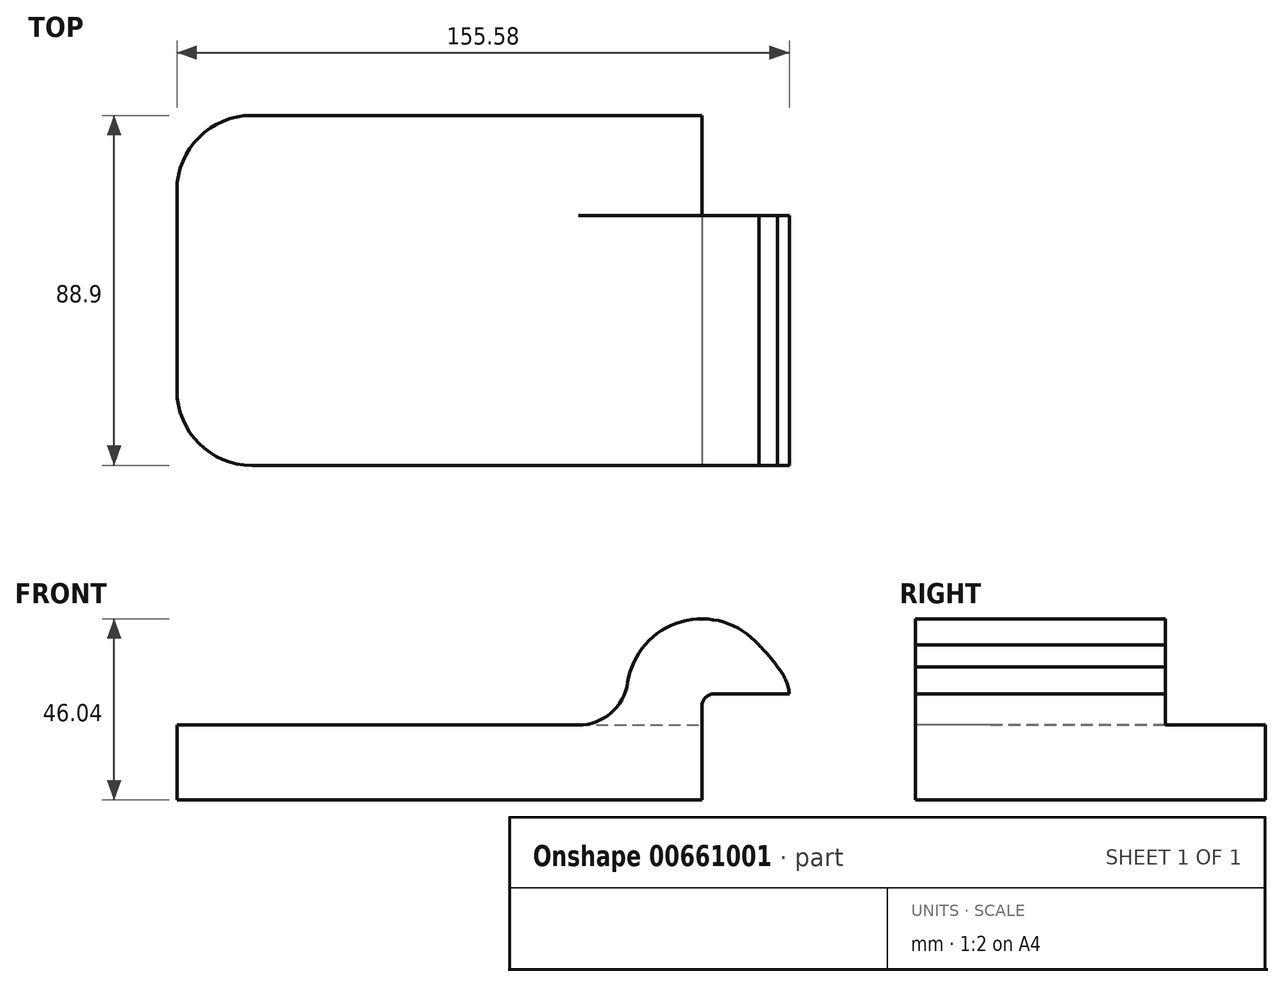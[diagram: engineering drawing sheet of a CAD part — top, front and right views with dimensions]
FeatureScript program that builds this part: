
annotation { "Feature Type Name" : "Feature", "Feature Type Description" : "" }
export const myFeature = defineFeature(function(context is Context, id is Id, definition is map)
    precondition{}
    {
        {
            var Q0;
            Q0=qCreatedBy(makeId("Top.planeOp"),FACE);
            var sketch = newSketch(context, id + "F0", { "sketchPlane" : qUnion([Q0])});
            skLineSegment(sketch, "E0", {"start": v(0, 0) * mm, "end": v(-25.4, 0) * mm, "construction": true});
            skLineSegment(sketch, "E1", {"start": v(-25.4, -63.5) * mm, "end": v(-139.7, -63.5) * mm});
            skLineSegment(sketch, "E2", {"start": v(-158.75, -44.45) * mm, "end": v(-158.75, 6.35) * mm});
            skLineSegment(sketch, "E3", {"start": v(-139.7, 25.4) * mm, "end": v(-25.4, 25.4) * mm});
            skLineSegment(sketch, "E4", {"start": v(-25.4, 25.4) * mm, "end": v(-25.4, -63.5) * mm});
            skPoint(sketch, "E5.visualSharp", {"position": v(-158.75, 25.4) * mm});
            skArc(sketch, "E5.filletArc", {"start": v(-139.7, 25.4) * mm, "mid": v(-153.17, 19.82) * mm, "end": v(-158.75, 6.35) * mm});
            skPoint(sketch, "E6.visualSharp", {"position": v(-158.75, -63.5) * mm});
            skArc(sketch, "E6.filletArc", {"start": v(-158.75, -44.45) * mm, "mid": v(-153.17, -57.92) * mm, "end": v(-139.7, -63.5) * mm});
            skPoint(sketch, "E7.orphan", {"position": v(-25.4, 0) * mm});
            skPoint(sketch, "E8.orphan", {"position": v(-3.17, -63.5) * mm});
            skSolve(sketch);
        }
        {
            var Q0;
            Q0=makeQuery(id+"F0.imprint","IMPRINT",FACE,{"disambiguationData":[TD([[makeQuery(id+"F0.imprint","IMPRINT",EDGE,{"derivedFrom":sQuery(id+"F0.wireOp",EDGE,"E1")}),-1.0]])]});
            extrude(context, id + "F1", {"entities" : qUnion([Q0]), "depth" : 19.05 * mm, "offsetDistance" : 25.4 * mm});
        }
        {
            var Q0;
            Q0=qCreatedBy(makeId("Front.planeOp"),FACE);
            cPlane(context, id + "F2", {"entities" : qUnion([Q0]), "cplaneType" : CPlaneType.OFFSET, "offset" : 63.5 * mm, "width" : 152.4 * mm, "height" : 152.4 * mm});
        }
        {
            var Q0;
            Q0=qCreatedBy(id+"F2.planeOp",FACE);
            var sketch = newSketch(context, id + "F3", { "sketchPlane" : qUnion([Q0])});
            skLineSegment(sketch, "E9.0", {"start": v(0, 0) * mm, "end": v(-25.4, 0) * mm, "construction": true});
            skLineSegment(sketch, "E10", {"start": v(-25.4, 19.05) * mm, "end": v(-25.4, 23.81) * mm});
            skLineSegment(sketch, "E11", {"start": v(-22.23, 26.99) * mm, "end": v(-3.17, 26.99) * mm});
            skPoint(sketch, "E12.visualSharp", {"position": v(-25.4, 26.99) * mm});
            skArc(sketch, "E12.filletArc", {"start": v(-22.23, 26.99) * mm, "mid": v(-24.47, 26.06) * mm, "end": v(-25.4, 23.81) * mm});
            skArc(sketch, "E13", {"start": v(-10.93, 39.38) * mm, "mid": v(-30.64, 45.3) * mm, "end": v(-44.23, 29.85) * mm});
            skArc(sketch, "E14", {"start": v(-3.18, 26.99) * mm, "mid": v(-4.17, 30.65) * mm, "end": v(-6.2, 33.85) * mm});
            skPoint(sketch, "E15.orphan", {"position": v(-25.4, 19.05) * mm});
            skPoint(sketch, "E16.visualSharp", {"position": v(-42.72, 19.05) * mm});
            skArc(sketch, "E16.filletArc", {"start": v(-56.8, 19.05) * mm, "mid": v(-48.51, 22.12) * mm, "end": v(-44.23, 29.85) * mm});
            skLineSegment(sketch, "E17", {"start": v(-56.8, 19.05) * mm, "end": v(-25.4, 19.05) * mm});
            skPoint(sketch, "E18.0.end.orphan", {"position": v(-139.7, 19.05) * mm});
            skArc(sketch, "E19", {"start": v(-6.2, 33.85) * mm, "mid": v(-8.44, 36.72) * mm, "end": v(-10.93, 39.38) * mm});
            skSolve(sketch);
        }
        {
            var Q0;
            Q0=makeQuery(id+"F3.imprint","IMPRINT",FACE,{"disambiguationData":[TD([[makeQuery(id+"F3.imprint","IMPRINT",EDGE,{"derivedFrom":sQuery(id+"F3.wireOp",EDGE,"E10")}),1.0]])]});
            extrude(context, id + "F4", {"entities" : qUnion([Q0]), "operationType" : NewBodyOperationType.ADD, "oppositeDirection" : true, "depth" : 63.5 * mm, "offsetDistance" : 25.4 * mm});
        }
    });
